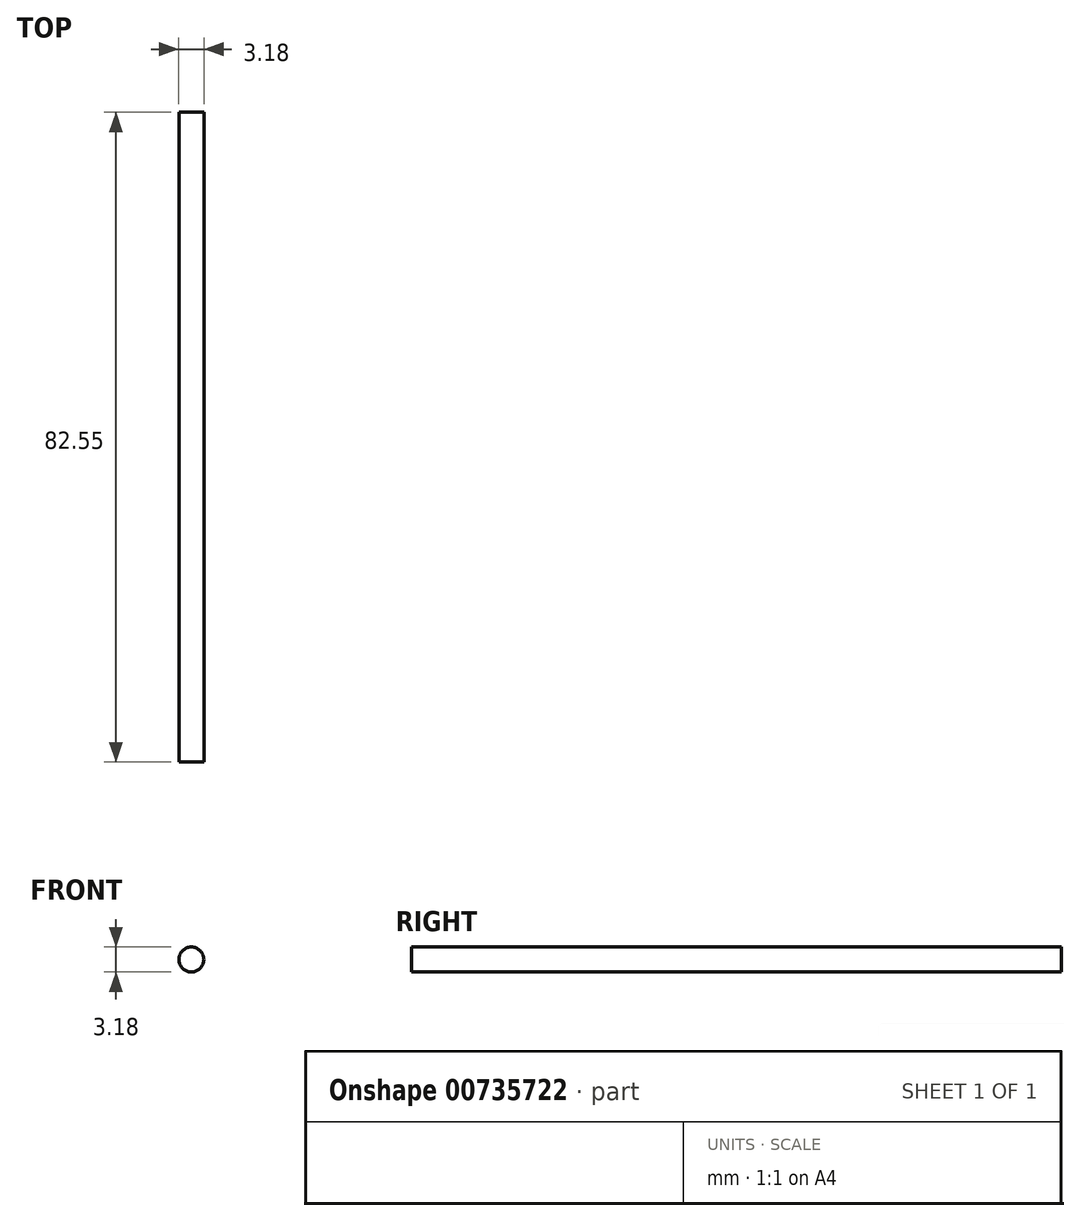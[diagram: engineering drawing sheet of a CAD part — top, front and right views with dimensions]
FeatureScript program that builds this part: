
annotation { "Feature Type Name" : "Feature", "Feature Type Description" : "" }
export const myFeature = defineFeature(function(context is Context, id is Id, definition is map)
    precondition{}
    {
        {
            var Q0;
            Q0=qCreatedBy(makeId("Front.planeOp"),FACE);
            var sketch = newSketch(context, id + "F0", { "sketchPlane" : qUnion([Q0])});
            skCircle(sketch, "E0", {"center": v(0, 0) * mm, "radius": 1.59 * mm});
            skSolve(sketch);
        }
        {
            var Q0;
            Q0=makeQuery(id+"F0.imprint","IMPRINT",FACE,{"disambiguationData":[TD([[makeQuery(id+"F0.imprint","IMPRINT",EDGE,{"derivedFrom":sQuery(id+"F0.wireOp",EDGE,"E0")}),1.0]])]});
            extrude(context, id + "F1", {"entities" : qUnion([Q0]), "depth" : 82.55 * mm, "offsetDistance" : 25.4 * mm});
        }
    });
